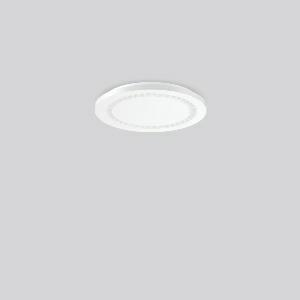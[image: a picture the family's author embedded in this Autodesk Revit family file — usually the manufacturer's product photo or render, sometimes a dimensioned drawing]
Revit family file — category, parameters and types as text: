
# Revit family: hemis_round_312185_002_3_8aee
name_source: partatom
category: Lighting Fixtures
units: mm (PartAtom-declared; Revit-internal decimal feet)

## family parameters
Cut with Voids When Loaded = No
Host = Face
Light Source = No
Part Type = Normal
Room Calculation Point = No
Round Connector Dimension = Use Diameter
Shared = No

## types (1)
- MultiLumen 1 (1 x LED Modul 840, 1950 lm, 4000)
    Apparent Load = 16 VA
    CIE Flux Codes = 87 99 100 100 100
    Color Rendering = 80
    Color Temperature = 4000
    Default Elevation = 1800 mm
    Description = Series: HEMIS round
Glare-free LED ceiling luminaire with optical lens system. Base: metal, powder-coated, with bayonet fixing. Housing: plastic (polycarbonate). Housing and diffuser are screwed together. Diffuser with optic lenses. Big terminal block; ideal for through-wiring. Sealing strip on the back of the luminaire connects seamlessly with the ceiling. Easy installation with Plug+Play plug connection. Thanks to RUG < 22 ideal for corridors, stairways, shops, schools, meeting rooms, rest areas. 
Colour: white
Diameter: 300 mm
Height: 33 mm
Lamp: LED
Socket: without socket
Colour temperature: 4000K
Colour rendering index (CRI): 80
System power: 16 W
Rated luminous flux: 1950 lm
Beam angle Down: 64°
Luminous efficiency: 122 lm/W
System power 2: 10 W
Rated luminous flux 2: 1250 lm
Luminous efficiency 2: 125 lm/W
Control gear: Regulated power supply
Protection class: I
Type of protection: IP 40
    Height = 33 mm
    Lamp = 1 x LED Modul 840
    Lamp Light Flux = 1950 lm
    Lamp count = 1
    Length = 300 mm
    Lifetime = 50000 h
    Luminous efficacy = 122 lm/W
    Manufacturer = RZB
    ModVariant = No
    Model = 312185.002.3
    Mounting Place = Ceiling
    Mounting Type = Surface mounted
    Number of Poles = 1
    OnlyDefault = Yes
    Power Factor = 1
    Product Name = HEMIS round
    Product group = Surface mounted modular luminaires
    ProductGroupID = 306
    Protection Class = Protection class I
    Protection Degree = Degree of protection
    RLX_Detail_Level = 1
    RLX_Emergency_Light_Flux = 0 lm
    RLX_Emergency_Type = 0
    RLX_Emergency_Type_DB = No
    RlxData = <blob elided: 40517 chars, md5=7d02ffce>
    Socket = socket
    Standby Power = 0 W
    System Light Flux = 1950 lm
    System Power = 16 W
    Type Comments = MultiLumen 1
    Type Image = 312185.002.jpg
    URL = http://relux.com
    VarID = multilumen_1
    Voltage = 0 V
    Weight = 0.00 kg
    Width = 0 mm  [stored 0 ft]

note: [stored X ft] marks values corroborated as IEEE doubles in the binary element streams (Revit-internal decimal feet)

## geometry (parser evidence)
native form markers: Blend x4, Sweep x9
no freeform markers — native parametric forms only
